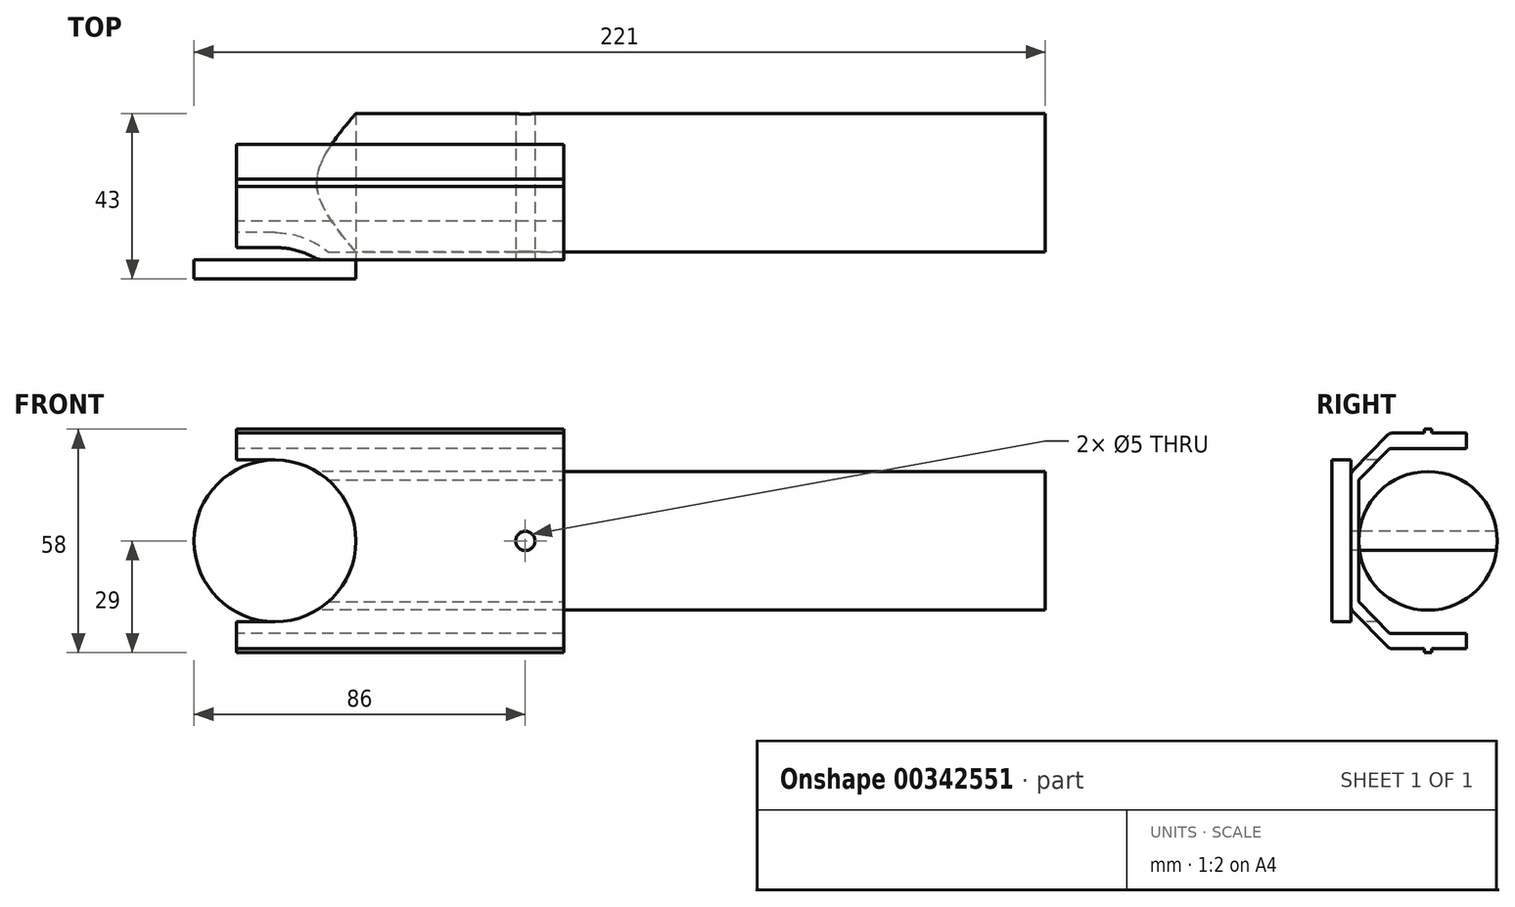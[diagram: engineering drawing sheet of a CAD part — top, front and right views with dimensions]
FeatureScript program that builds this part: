
annotation { "Feature Type Name" : "Feature", "Feature Type Description" : "" }
export const myFeature = defineFeature(function(context is Context, id is Id, definition is map)
    precondition{}
    {
        {
            var Q0;
            Q0=qCreatedBy(makeId("Front.planeOp"),FACE);
            var sketch = newSketch(context, id + "F0", { "sketchPlane" : qUnion([Q0])});
            skCircle(sketch, "E0", {"center": v(0, 0) * mm, "radius": 21 * mm});
            skSolve(sketch);
        }
        {
            var Q0;
            Q0 = qSketchRegion(id + "F0", true);
            extrude(context, id + "F1", {"entities" : qUnion([Q0]), "endBound" : BoundingType.SYMMETRIC, "depth" : 50 * mm});
        }
        {
            var Q0;
            Q0=qCreatedBy(makeId("Right.planeOp"),FACE);
            var sketch = newSketch(context, id + "F2", { "sketchPlane" : qUnion([Q0])});
            skCircle(sketch, "E1", {"center": v(0, 0) * mm, "radius": 18 * mm});
            skSolve(sketch);
        }
        {
            var Q0;
            Q0 = qSketchRegion(id + "F2", true);
            extrude(context, id + "F3", {"entities" : qUnion([Q0]), "operationType" : NewBodyOperationType.ADD, "depth" : 200 * mm});
        }
        {
            var Q0;
            Q0=qCreatedBy(makeId("Front.planeOp"),FACE);
            cPlane(context, id + "F4", {"entities" : qUnion([Q0]), "cplaneType" : CPlaneType.OFFSET, "offset" : 18 * mm, "width" : 150 * mm, "height" : 150 * mm});
        }
        {
            var Q0;
            Q0=qCreatedBy(id+"F4.planeOp",FACE);
            var sketch = newSketch(context, id + "F5", { "sketchPlane" : qUnion([Q0])});
            skCircle(sketch, "E2", {"center": v(65, 0) * mm, "radius": 2.5 * mm});
            skSolve(sketch);
        }
        {
            var Q0;
            Q0 = qSketchRegion(id + "F5", true);
            extrude(context, id + "F6", {"entities" : qUnion([Q0]), "operationType" : NewBodyOperationType.REMOVE, "oppositeDirection" : true, "depth" : 30 * mm});
        }
        {
            var Q0;
            Q0=qCreatedBy(makeId("Right.planeOp"),FACE);
            cPlane(context, id + "F7", {"entities" : qUnion([Q0]), "cplaneType" : CPlaneType.OFFSET, "offset" : 10 * mm, "oppositeDirection" : true, "width" : 150 * mm, "height" : 150 * mm});
        }
        {
            var Q0;
            Q0=qCreatedBy(id+"F7.planeOp",FACE);
            var sketch = newSketch(context, id + "F8", { "sketchPlane" : qUnion([Q0])});
            skLineSegment(sketch, "E3", {"start": v(0, 48.61) * mm, "end": v(0, -58.43) * mm});
            skLineSegment(sketch, "E4", {"start": v(-60.37, 0) * mm, "end": v(50.93, 0) * mm});
            skLineSegment(sketch, "E5", {"start": v(0, 24) * mm, "end": v(-10, 24) * mm});
            skLineSegment(sketch, "E6", {"start": v(-10, 24) * mm, "end": v(-10, 28) * mm});
            skLineSegment(sketch, "E7", {"start": v(-10, 28) * mm, "end": v(-1, 28) * mm});
            skLineSegment(sketch, "E8", {"start": v(-1, 28) * mm, "end": v(-1, 29) * mm});
            skLineSegment(sketch, "E9", {"start": v(-1, 29) * mm, "end": v(0, 29) * mm});
            skLineSegment(sketch, "E10.MirrorCS", {"start": v(10, 28) * mm, "end": v(1, 28) * mm});
            skLineSegment(sketch, "E11.MirrorCS", {"start": v(10, 24) * mm, "end": v(10, 28) * mm});
            skLineSegment(sketch, "E12.MirrorCS", {"start": v(0, 24) * mm, "end": v(10, 24) * mm});
            skLineSegment(sketch, "E13.MirrorCS", {"start": v(1, 29) * mm, "end": v(0, 29) * mm});
            skLineSegment(sketch, "E14.MirrorCS", {"start": v(1, 28) * mm, "end": v(1, 29) * mm});
            skLineSegment(sketch, "E15.MirrorCS", {"start": v(1, -28) * mm, "end": v(1, -29) * mm});
            skLineSegment(sketch, "E16.MirrorCS", {"start": v(1, -29) * mm, "end": v(0, -29) * mm});
            skLineSegment(sketch, "E17.MirrorCS", {"start": v(-1, -28) * mm, "end": v(-1, -29) * mm});
            skLineSegment(sketch, "E18.MirrorCS", {"start": v(-1, -29) * mm, "end": v(0, -29) * mm});
            skLineSegment(sketch, "E19.MirrorCS", {"start": v(10, -24) * mm, "end": v(10, -28) * mm});
            skLineSegment(sketch, "E20.MirrorCS", {"start": v(0, -24) * mm, "end": v(10, -24) * mm});
            skLineSegment(sketch, "E21.MirrorCS", {"start": v(0, -24) * mm, "end": v(-10, -24) * mm});
            skLineSegment(sketch, "E22.MirrorCS", {"start": v(-10, -24) * mm, "end": v(-10, -28) * mm});
            skLineSegment(sketch, "E23.MirrorCS", {"start": v(-10, -28) * mm, "end": v(-1, -28) * mm});
            skLineSegment(sketch, "E24.MirrorCS", {"start": v(10, -28) * mm, "end": v(1, -28) * mm});
            skSolve(sketch);
        }
        {
            var Q0;
            {var subQ0=sQuery(id+"F8.wireOp",EDGE,"E5");Q0=makeQuery(id+"F8.imprint","IMPRINT",FACE,{"disambiguationData":[TD([[makeQuery(id+"F8.imprint","IMPRINT",EDGE,{"derivedFrom":subQ0}),-1.0]])]});}
            var Q1;
            Q1=makeQuery(id+"F8.imprint","IMPRINT",FACE,{"disambiguationData":[TD([[makeQuery(id+"F8.imprint","IMPRINT",EDGE,{"derivedFrom":sQuery(id+"F8.wireOp",EDGE,"E10.MirrorCS")}),1.0]])]});
            var Q2;
            Q2=makeQuery(id+"F8.imprint","IMPRINT",FACE,{"disambiguationData":[TD([[makeQuery(id+"F8.imprint","IMPRINT",EDGE,{"derivedFrom":sQuery(id+"F8.wireOp",EDGE,"E17.MirrorCS")}),1.0]])]});
            var Q3;
            Q3=makeQuery(id+"F8.imprint","IMPRINT",FACE,{"disambiguationData":[TD([[makeQuery(id+"F8.imprint","IMPRINT",EDGE,{"derivedFrom":sQuery(id+"F8.wireOp",EDGE,"E15.MirrorCS")}),-1.0]])]});
            extrude(context, id + "F9", {"entities" : qUnion([Q0, Q1, Q2, Q3]), "depth" : 85 * mm});
        }
        {
            var Q0;
            Q0=makeQuery(id+"F9.opExtrude","CAP_FACE",FACE,{"disambiguationData":[OSD([sQuery(id+"F8.wireOp",EDGE,"E5"),sQuery(id+"F8.wireOp",EDGE,"E6"),sQuery(id+"F8.wireOp",EDGE,"E7"),sQuery(id+"F8.wireOp",EDGE,"E8"),sQuery(id+"F8.wireOp",EDGE,"E9"),sQuery(id+"F8.wireOp",EDGE,"E10.MirrorCS"),sQuery(id+"F8.wireOp",EDGE,"E11.MirrorCS"),sQuery(id+"F8.wireOp",EDGE,"E12.MirrorCS"),sQuery(id+"F8.wireOp",EDGE,"E13.MirrorCS"),sQuery(id+"F8.wireOp",EDGE,"E14.MirrorCS")])],"isStart":false});
            var sketch = newSketch(context, id + "F10", { "sketchPlane" : qUnion([Q0])});
            skLineSegment(sketch, "E25", {"start": v(-18, 0) * mm, "end": v(-18, 15.79) * mm});
            skLineSegment(sketch, "E26", {"start": v(-18, 15.79) * mm, "end": v(-10, 24) * mm});
            skLineSegment(sketch, "E27", {"start": v(-56.87, 0) * mm, "end": v(48.34, 0) * mm});
            skLineSegment(sketch, "E28", {"start": v(-10, 28) * mm, "end": v(-20, 17.73) * mm});
            skLineSegment(sketch, "E29", {"start": v(-20, 17.73) * mm, "end": v(-20, 0) * mm});
            skLineSegment(sketch, "E30.MirrorCS", {"start": v(-20, -17.73) * mm, "end": v(-20, 0) * mm});
            skLineSegment(sketch, "E31.MirrorCS", {"start": v(-10, -28) * mm, "end": v(-20, -17.73) * mm});
            skLineSegment(sketch, "E32.MirrorCS", {"start": v(-18, -15.79) * mm, "end": v(-10, -24) * mm});
            skLineSegment(sketch, "E33.MirrorCS", {"start": v(-18, 0) * mm, "end": v(-18, -15.79) * mm});
            skLineSegment(sketch, "E34", {"start": v(-10, -28) * mm, "end": v(-10, -24) * mm});
            skSolve(sketch);
        }
        {
            var Q0;
            {var subQ0=sQuery(id+"F10.wireOp",EDGE,"E30.MirrorCS");Q0=makeQuery(id+"F10.imprint","IMPRINT",FACE,{"disambiguationData":[TD([[makeQuery(id+"F10.imprint","IMPRINT",EDGE,{"derivedFrom":subQ0}),-1.0]])]});}
            var Q1;
            {var subQ1=sQuery(id+"F10.wireOp",EDGE,"E25");Q1=makeQuery(id+"F10.imprint","IMPRINT",FACE,{"disambiguationData":[TD([[makeQuery(id+"F10.imprint","IMPRINT",EDGE,{"derivedFrom":subQ1}),1.0]])]});}
            extrude(context, id + "F11", {"entities" : qUnion([Q0, Q1]), "oppositeDirection" : true, "depth" : 85 * mm});
        }
        {
            var Q0;
            Q0=makeQuery(id+"F11.opExtrude","SWEPT_FACE",FACE,{"disambiguationData":[OSD([sQuery(id+"F10.wireOp",EDGE,"E29"),sQuery(id+"F10.wireOp",EDGE,"E30.MirrorCS")])]});
            var sketch = newSketch(context, id + "F12", { "sketchPlane" : qUnion([Q0])});
            skCircle(sketch, "E35", {"center": v(0, 0) * mm, "radius": 21 * mm});
            skLineSegment(sketch, "E36", {"start": v(0, 21) * mm, "end": v(-10, 21) * mm});
            skLineSegment(sketch, "E37", {"start": v(-10, 21) * mm, "end": v(-10, 18.47) * mm});
            skLineSegment(sketch, "E38", {"start": v(0, -21) * mm, "end": v(-10, -21) * mm});
            skLineSegment(sketch, "E39", {"start": v(-10, -21) * mm, "end": v(-10, -18.47) * mm});
            skSolve(sketch);
        }
        {
            var Q0;
            Q0 = qSketchRegion(id + "F12", true);
            extrude(context, id + "F13", {"entities" : qUnion([Q0]), "operationType" : NewBodyOperationType.REMOVE, "endBound" : BoundingType.THROUGH_ALL, "oppositeDirection" : true, "depth" : 30 * mm});
        }
        {
            var Q0;
            Q0=makeQuery(id+"F11.opExtrude","SWEPT_FACE",FACE,{"disambiguationData":[OSD([sQuery(id+"F10.wireOp",EDGE,"E29"),sQuery(id+"F10.wireOp",EDGE,"E30.MirrorCS")])]});
            var sketch = newSketch(context, id + "F14", { "sketchPlane" : qUnion([Q0])});
            skCircle(sketch, "E40", {"center": v(65, 0) * mm, "radius": 2.5 * mm});
            skSolve(sketch);
        }
        {
            var Q0;
            Q0=makeQuery(id+"F14.imprint","IMPRINT",FACE,{"disambiguationData":[TD([[makeQuery(id+"F14.imprint","IMPRINT",EDGE,{"derivedFrom":sQuery(id+"F14.wireOp",EDGE,"E40")}),1.0]])]});
            extrude(context, id + "F15", {"entities" : qUnion([Q0]), "operationType" : NewBodyOperationType.REMOVE, "endBound" : BoundingType.THROUGH_ALL, "oppositeDirection" : true, "depth" : 25 * mm});
        }
        {
            var Q0;
            Q0=makeQuery(id+"F9.opExtrude","SWEPT_BODY",BODY,{"disambiguationData":[OSD([sQuery(id+"F8.wireOp",EDGE,"E5"),sQuery(id+"F8.wireOp",EDGE,"E6"),sQuery(id+"F8.wireOp",EDGE,"E7"),sQuery(id+"F8.wireOp",EDGE,"E8"),sQuery(id+"F8.wireOp",EDGE,"E9"),sQuery(id+"F8.wireOp",EDGE,"E10.MirrorCS"),sQuery(id+"F8.wireOp",EDGE,"E11.MirrorCS"),sQuery(id+"F8.wireOp",EDGE,"E12.MirrorCS"),sQuery(id+"F8.wireOp",EDGE,"E13.MirrorCS"),sQuery(id+"F8.wireOp",EDGE,"E14.MirrorCS")])]});
            var Q1;
            Q1=makeQuery(id+"F9.opExtrude","SWEPT_BODY",BODY,{"disambiguationData":[OSD([sQuery(id+"F8.wireOp",EDGE,"E15.MirrorCS"),sQuery(id+"F8.wireOp",EDGE,"E16.MirrorCS"),sQuery(id+"F8.wireOp",EDGE,"E17.MirrorCS"),sQuery(id+"F8.wireOp",EDGE,"E18.MirrorCS"),sQuery(id+"F8.wireOp",EDGE,"E19.MirrorCS"),sQuery(id+"F8.wireOp",EDGE,"E20.MirrorCS"),sQuery(id+"F8.wireOp",EDGE,"E21.MirrorCS"),sQuery(id+"F8.wireOp",EDGE,"E22.MirrorCS"),sQuery(id+"F8.wireOp",EDGE,"E23.MirrorCS"),sQuery(id+"F8.wireOp",EDGE,"E24.MirrorCS")])]});
            var Q2;
            Q2=makeQuery(id+"F11.opExtrude","SWEPT_BODY",BODY,{"disambiguationData":[OSD([sQuery(id+"F8.wireOp",EDGE,"E6"),sQuery(id+"F10.wireOp",EDGE,"E25"),sQuery(id+"F10.wireOp",EDGE,"E26"),sQuery(id+"F10.wireOp",EDGE,"E28"),sQuery(id+"F10.wireOp",EDGE,"E29"),sQuery(id+"F10.wireOp",EDGE,"E30.MirrorCS"),sQuery(id+"F10.wireOp",EDGE,"E31.MirrorCS"),sQuery(id+"F10.wireOp",EDGE,"E32.MirrorCS"),sQuery(id+"F10.wireOp",EDGE,"E33.MirrorCS"),sQuery(id+"F10.wireOp",EDGE,"E34")])]});
            booleanBodies(context, id + "F16", {"operationType" : BooleanOperationType.UNION, "tools" : qUnion([Q0, Q1, Q2])});
        }
        {
            var Q0;
            {var subQ0=sQuery(id+"F8.wireOp",EDGE,"E7");var subQ1=sQuery(id+"F8.wireOp",EDGE,"E6");Q0=makeQuery(id+"F16.opBoolean","MERGE",EDGE,{"derivedFrom":[makeQuery(id+"F9.opExtrude","SWEPT_EDGE",EDGE,{"disambiguationData":[OSD([subQ1,subQ0])]}),makeQuery(id+"F11.opExtrude","SWEPT_EDGE",EDGE,{"disambiguationData":[OSD([subQ1,subQ0,sQuery(id+"F10.wireOp",EDGE,"E28")])]})]});}
            var Q1;
            Q1=makeQuery(id+"F11.opExtrude","SWEPT_EDGE",EDGE,{"disambiguationData":[OSD([sQuery(id+"F10.wireOp",EDGE,"E28"),sQuery(id+"F10.wireOp",EDGE,"E29")])]});
            var Q2;
            Q2=makeQuery(id+"F11.opExtrude","SWEPT_EDGE",EDGE,{"disambiguationData":[OSD([sQuery(id+"F10.wireOp",EDGE,"E30.MirrorCS"),sQuery(id+"F10.wireOp",EDGE,"E31.MirrorCS")])]});
            var Q3;
            Q3=makeQuery(id+"F16.opBoolean","MERGE",EDGE,{"derivedFrom":[makeQuery(id+"F9.opExtrude","SWEPT_EDGE",EDGE,{"disambiguationData":[OSD([sQuery(id+"F8.wireOp",EDGE,"E22.MirrorCS"),sQuery(id+"F8.wireOp",EDGE,"E23.MirrorCS")])]}),makeQuery(id+"F11.opExtrude","SWEPT_EDGE",EDGE,{"disambiguationData":[OSD([sQuery(id+"F10.wireOp",EDGE,"E31.MirrorCS"),sQuery(id+"F10.wireOp",EDGE,"E34")])]})]});
            fillet(context, id + "F17", {"entities" : qUnion([Q0, Q1, Q2, Q3]), "radius" : 2 * mm, "tangentPropagation" : true, "allowEdgeOverflow" : false});
        }
    });
